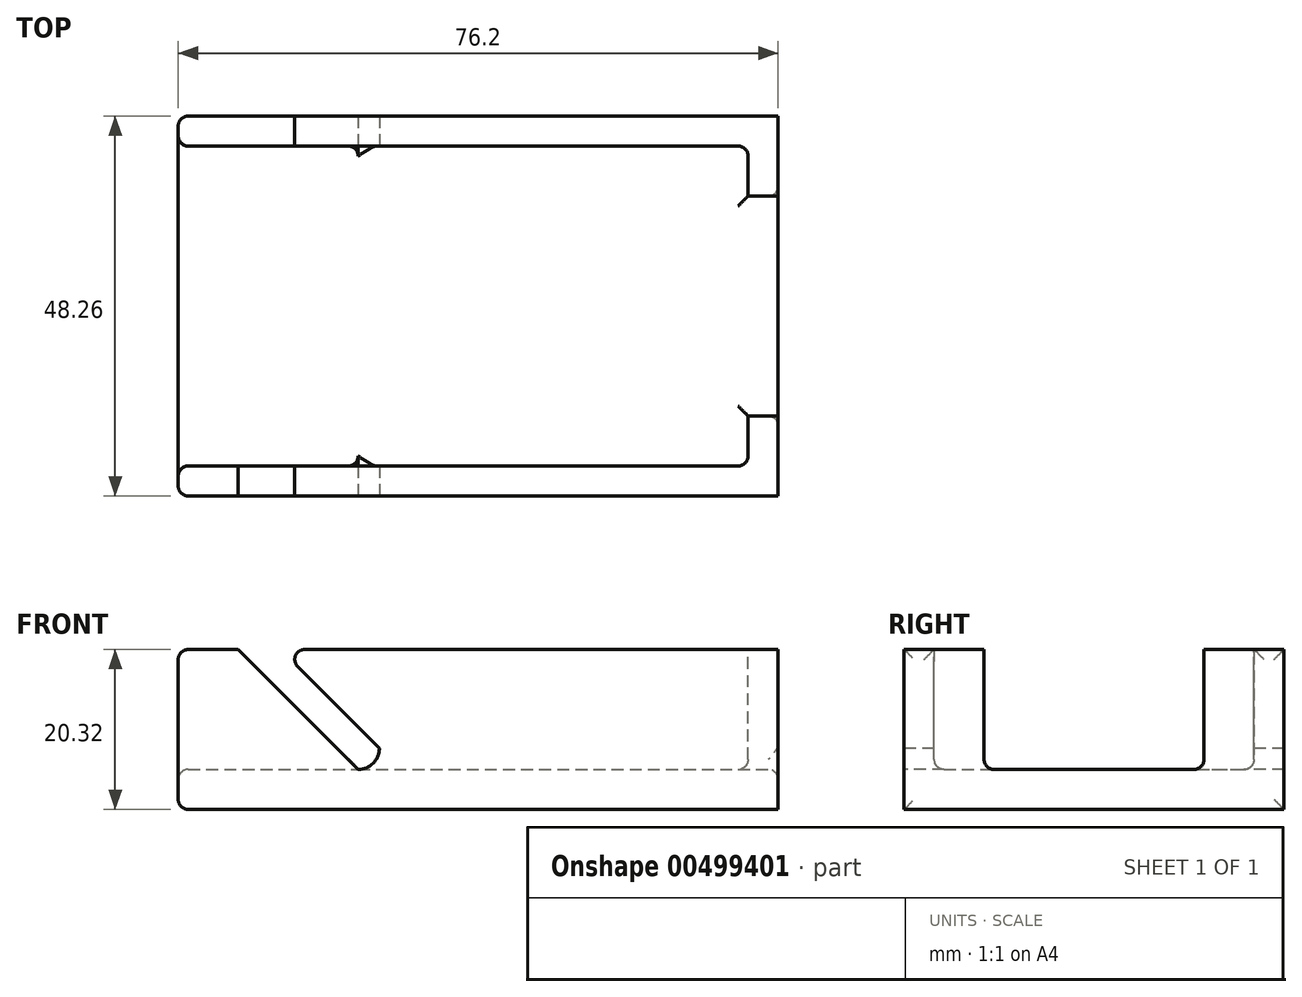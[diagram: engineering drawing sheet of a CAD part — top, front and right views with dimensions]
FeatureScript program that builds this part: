
annotation { "Feature Type Name" : "Feature", "Feature Type Description" : "" }
export const myFeature = defineFeature(function(context is Context, id is Id, definition is map)
    precondition{}
    {
        {
            var Q0;
            Q0=qCreatedBy(makeId("Top.planeOp"),FACE);
            var sketch = newSketch(context, id + "F0", { "sketchPlane" : qUnion([Q0])});
            skLineSegment(sketch, "E0", {"start": v(0, 0) * mm, "end": v(0, 24.13) * mm});
            skLineSegment(sketch, "E1", {"start": v(0, 24.13) * mm, "end": v(38.1, 24.13) * mm});
            skLineSegment(sketch, "E2", {"start": v(38.1, 24.13) * mm, "end": v(38.1, -24.13) * mm});
            skLineSegment(sketch, "E3", {"start": v(38.1, -24.13) * mm, "end": v(0, -24.13) * mm});
            skLineSegment(sketch, "E4", {"start": v(0, -24.13) * mm, "end": v(0, 0) * mm});
            skSolve(sketch);
        }
        {
            var Q0;
            Q0=makeQuery(id+"F0.imprint","IMPRINT",FACE,{"disambiguationData":[TD([[makeQuery(id+"F0.imprint","IMPRINT",EDGE,{"derivedFrom":sQuery(id+"F0.wireOp",EDGE,"E0")}),-1.0]])]});
            extrude(context, id + "F1", {"entities" : qUnion([Q0]), "depth" : 20.32 * mm});
        }
        {
            var Q0;
            Q0=makeQuery(id+"F1.opExtrude","CAP_FACE",FACE,{"disambiguationData":[OSD([sQuery(id+"F0.wireOp",EDGE,"E0"),sQuery(id+"F0.wireOp",EDGE,"E1"),sQuery(id+"F0.wireOp",EDGE,"E2"),sQuery(id+"F0.wireOp",EDGE,"E3"),sQuery(id+"F0.wireOp",EDGE,"E4")])],"isStart":false});
            var sketch = newSketch(context, id + "F2", { "sketchPlane" : qUnion([Q0])});
            skLineSegment(sketch, "E5.bottom", {"start": v(0, 0) * mm, "end": v(34.3, 0) * mm});
            skLineSegment(sketch, "E5.top", {"start": v(0, 20.32) * mm, "end": v(34.3, 20.32) * mm});
            skLineSegment(sketch, "E5.left", {"start": v(0, 0) * mm, "end": v(0, 20.32) * mm});
            skLineSegment(sketch, "E5.right", {"start": v(34.3, 0) * mm, "end": v(34.3, 20.32) * mm});
            skLineSegment(sketch, "E6", {"start": v(0, 0) * mm, "end": v(0, -20.32) * mm});
            skLineSegment(sketch, "E7", {"start": v(0, -20.32) * mm, "end": v(34.3, -20.32) * mm});
            skLineSegment(sketch, "E8", {"start": v(34.3, -20.32) * mm, "end": v(34.3, 0) * mm});
            skSolve(sketch);
        }
        {
            var Q0;
            Q0 = qSketchRegion(id + "F2", true);
            extrude(context, id + "F3", {"entities" : qUnion([Q0]), "operationType" : NewBodyOperationType.REMOVE, "oppositeDirection" : true, "depth" : 15.24 * mm});
        }
        {
            var Q0;
            Q0=makeQuery(id+"F1.opExtrude","SWEPT_FACE",FACE,{"disambiguationData":[OSD([sQuery(id+"F0.wireOp",EDGE,"E0"),sQuery(id+"F0.wireOp",EDGE,"E4")])]});
            extrude(context, id + "F4", {"entities" : qUnion([Q0]), "operationType" : NewBodyOperationType.ADD, "depth" : 38.1 * mm});
        }
        {
            var Q0;
            {var subQ0=sQuery(id+"F0.wireOp",EDGE,"E3");Q0=makeQuery(id+"F4.boolean.opBoolean","MERGE",FACE,{"derivedFrom":[makeQuery(id+"F1.opExtrude","SWEPT_FACE",FACE,{"disambiguationData":[OSD([subQ0])]}),makeQuery(id+"F4.opExtrude","SWEPT_FACE",FACE,{"disambiguationData":[OSD([subQ0,sQuery(id+"F0.wireOp",EDGE,"E4")])]})]});}
            var sketch = newSketch(context, id + "F5", { "sketchPlane" : qUnion([Q0])});
            skLineSegment(sketch, "E9", {"start": v(-38.1, 20.32) * mm, "end": v(-30.48, 20.32) * mm});
            skLineSegment(sketch, "E10", {"start": v(-30.48, 20.32) * mm, "end": v(-15.24, 5.08) * mm});
            skLineSegment(sketch, "E11", {"start": v(-12.55, 7.77) * mm, "end": v(-25.1, 20.32) * mm});
            skLineSegment(sketch, "E12", {"start": v(-25.1, 20.32) * mm, "end": v(-30.48, 20.32) * mm});
            skArc(sketch, "E13", {"start": v(-15.24, 5.08) * mm, "mid": v(-13.33, 5.87) * mm, "end": v(-12.55, 7.77) * mm});
            skLineSegment(sketch, "E14", {"start": v(-30.48, 20.32) * mm, "end": v(-25.1, 20.32) * mm});
            skSolve(sketch);
        }
        {
            var Q0;
            Q0=makeQuery(id+"F5.imprint","IMPRINT",FACE,{"disambiguationData":[TD([[makeQuery(id+"F5.imprint","IMPRINT",EDGE,{"derivedFrom":sQuery(id+"F5.wireOp",EDGE,"E10")}),1.0]])]});
            extrude(context, id + "F6", {"entities" : qUnion([Q0]), "operationType" : NewBodyOperationType.REMOVE, "oppositeDirection" : true, "depth" : 76.2 * mm});
        }
        {
            var Q0;
            Q0=makeQuery(id+"F1.opExtrude","SWEPT_FACE",FACE,{"disambiguationData":[OSD([sQuery(id+"F0.wireOp",EDGE,"E2")])]});
            var sketch = newSketch(context, id + "F7", { "sketchPlane" : qUnion([Q0])});
            skLineSegment(sketch, "E15.bottom", {"start": v(-13.97, 20.32) * mm, "end": v(13.97, 20.32) * mm});
            skLineSegment(sketch, "E15.top", {"start": v(-13.97, 5.08) * mm, "end": v(13.97, 5.08) * mm});
            skLineSegment(sketch, "E15.left", {"start": v(-13.97, 20.32) * mm, "end": v(-13.97, 5.08) * mm});
            skLineSegment(sketch, "E15.right", {"start": v(13.97, 20.32) * mm, "end": v(13.97, 5.08) * mm});
            skSolve(sketch);
        }
        {
            var Q0;
            Q0 = qSketchRegion(id + "F7", true);
            extrude(context, id + "F8", {"entities" : qUnion([Q0]), "operationType" : NewBodyOperationType.REMOVE, "oppositeDirection" : true, "depth" : 25.4 * mm});
        }
        {
            var Q0;
            {var subQ0=sQuery(id+"F2.wireOp",EDGE,"E6");var subQ1=sQuery(id+"F2.wireOp",EDGE,"E5.left");Q0=makeQuery(id+"F4.boolean.opBoolean","MERGE",FACE,{"derivedFrom":[makeQuery(id+"F3.boolean.opBoolean","COPY",FACE,{"derivedFrom":makeQuery(id+"F3.opExtrude","CAP_FACE",FACE,{"disambiguationData":[OSD([sQuery(id+"F2.wireOp",EDGE,"E5.top"),subQ1,sQuery(id+"F2.wireOp",EDGE,"E5.right"),subQ0,sQuery(id+"F2.wireOp",EDGE,"E7"),sQuery(id+"F2.wireOp",EDGE,"E8")])],"isStart":false})}),makeQuery(id+"F4.opExtrude","SWEPT_FACE",FACE,{"disambiguationData":[OSD([subQ1,subQ0])]})]});}
            var Q1;
            Q1=makeQuery(id+"F3.boolean.opBoolean","COPY",EDGE,{"derivedFrom":makeQuery(id+"F3.opExtrude","SWEPT_EDGE",EDGE,{"disambiguationData":[OSD([sQuery(id+"F2.wireOp",EDGE,"E5.top"),sQuery(id+"F2.wireOp",EDGE,"E5.right")])]})});
            var Q2;
            Q2=makeQuery(id+"F3.boolean.opBoolean","COPY",EDGE,{"derivedFrom":makeQuery(id+"F3.opExtrude","SWEPT_EDGE",EDGE,{"disambiguationData":[OSD([sQuery(id+"F2.wireOp",EDGE,"E7"),sQuery(id+"F2.wireOp",EDGE,"E8")])]})});
            var Q3;
            {var subQ0=sQuery(id+"F0.wireOp",EDGE,"E1");var subQ4=sQuery(id+"F0.wireOp",EDGE,"E4");var subQ5=sQuery(id+"F0.wireOp",EDGE,"E3");var subQ9=makeQuery(id+"F1.opExtrude","SWEPT_FACE",FACE,{"disambiguationData":[OSD([subQ0])]});var subQ10=sQuery(id+"F5.wireOp",EDGE,"E11");Q3=makeQuery(id+"F6.boolean.opBoolean","COPY",EDGE,{"disambiguationData":[TD([subQ9])],"derivedFrom":makeQuery(id+"F6.opExtrude","SWEPT_EDGE",EDGE,{"disambiguationData":[OSD([subQ5,subQ4,subQ10,sQuery(id+"F5.wireOp",EDGE,"E14")])]})});}
            var Q4;
            {var subQ0=sQuery(id+"F0.wireOp",EDGE,"E1");var subQ9=makeQuery(id+"F1.opExtrude","SWEPT_FACE",FACE,{"disambiguationData":[OSD([subQ0])]});var subQ10=sQuery(id+"F5.wireOp",EDGE,"E10");Q4=makeQuery(id+"F6.boolean.opBoolean","COPY",EDGE,{"disambiguationData":[TD([subQ9])],"derivedFrom":makeQuery(id+"F6.opExtrude","SWEPT_EDGE",EDGE,{"disambiguationData":[OSD([sQuery(id+"F5.wireOp",EDGE,"E9"),subQ10,sQuery(id+"F5.wireOp",EDGE,"E14")])]})});}
            var Q5;
            {var subQ2=sQuery(id+"F0.wireOp",EDGE,"E3");var subQ3=makeQuery(id+"F1.opExtrude","SWEPT_FACE",FACE,{"disambiguationData":[OSD([subQ2])]});var subQ4=sQuery(id+"F0.wireOp",EDGE,"E4");var subQ10=sQuery(id+"F5.wireOp",EDGE,"E11");Q5=makeQuery(id+"F6.boolean.opBoolean","COPY",EDGE,{"disambiguationData":[TD([subQ3])],"derivedFrom":makeQuery(id+"F6.opExtrude","SWEPT_EDGE",EDGE,{"disambiguationData":[OSD([subQ2,subQ4,subQ10,sQuery(id+"F5.wireOp",EDGE,"E14")])]})});}
            var Q6;
            {var subQ2=sQuery(id+"F0.wireOp",EDGE,"E3");var subQ3=makeQuery(id+"F1.opExtrude","SWEPT_FACE",FACE,{"disambiguationData":[OSD([subQ2])]});var subQ10=sQuery(id+"F5.wireOp",EDGE,"E10");Q6=makeQuery(id+"F6.boolean.opBoolean","COPY",EDGE,{"disambiguationData":[TD([subQ3])],"derivedFrom":makeQuery(id+"F6.opExtrude","SWEPT_EDGE",EDGE,{"disambiguationData":[OSD([sQuery(id+"F5.wireOp",EDGE,"E9"),subQ10,sQuery(id+"F5.wireOp",EDGE,"E14")])]})});}
            var Q7;
            Q7=makeQuery(id+"F4.opExtrude","CAP_FACE",FACE,{"disambiguationData":[OSD([sQuery(id+"F0.wireOp",EDGE,"E0"),sQuery(id+"F0.wireOp",EDGE,"E4")])],"isStart":false});
            fillet(context, id + "F9", {"entities" : qUnion([Q0, Q1, Q2, Q3, Q4, Q5, Q6, Q7]), "radius" : 1.27 * mm, "tangentPropagation" : true, "allowEdgeOverflow" : false});
        }
    });
